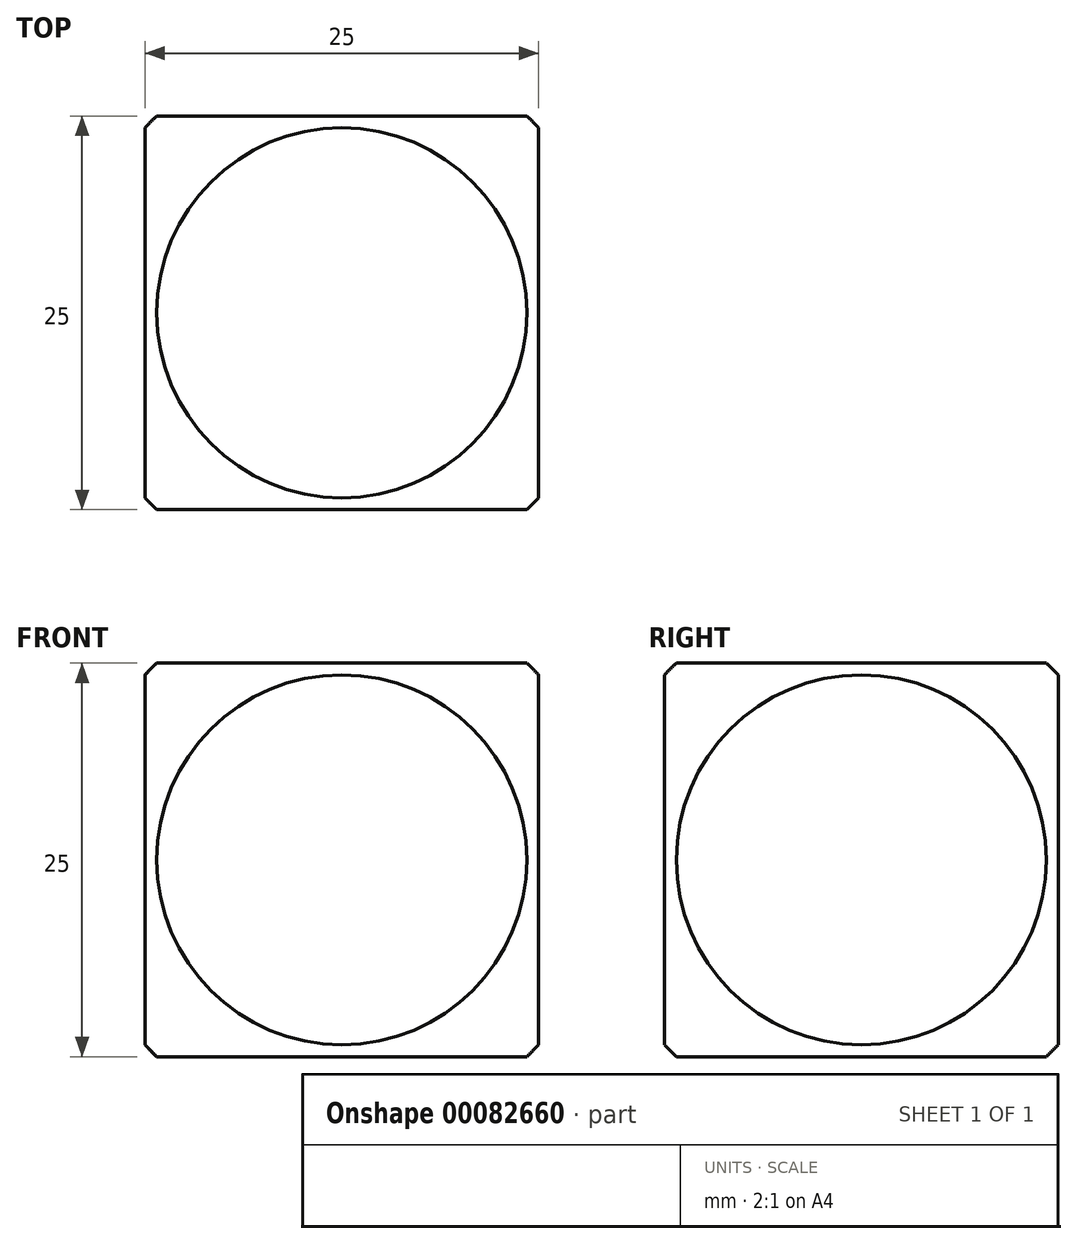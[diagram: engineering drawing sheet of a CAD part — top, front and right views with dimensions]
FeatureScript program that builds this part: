
annotation { "Feature Type Name" : "Feature", "Feature Type Description" : "" }
export const myFeature = defineFeature(function(context is Context, id is Id, definition is map)
    precondition{}
    {
        {
            var Q0;
            Q0=qCreatedBy(makeId("Front.planeOp"),FACE);
            var sketch = newSketch(context, id + "F0", { "sketchPlane" : qUnion([Q0])});
            skLineSegment(sketch, "E0.bottom", {"start": v(12.5, 12.5) * mm, "end": v(-12.5, 12.5) * mm});
            skLineSegment(sketch, "E0.top", {"start": v(12.5, -12.5) * mm, "end": v(-12.5, -12.5) * mm});
            skLineSegment(sketch, "E0.left", {"start": v(12.5, 12.5) * mm, "end": v(12.5, -12.5) * mm});
            skLineSegment(sketch, "E0.right", {"start": v(-12.5, 12.5) * mm, "end": v(-12.5, -12.5) * mm});
            skPoint(sketch, "E0.middle", {"position": v(0, 0) * mm});
            skSolve(sketch);
        }
        {
            var Q0;
            Q0 = qSketchRegion(id + "F0", true);
            extrude(context, id + "F1", {"entities" : qUnion([Q0]), "endBound" : BoundingType.SYMMETRIC, "depth" : 25 * mm});
        }
        {
            var Q0;
            Q0=qCreatedBy(makeId("Front.planeOp"),FACE);
            var sketch = newSketch(context, id + "F2", { "sketchPlane" : qUnion([Q0])});
            skLineSegment(sketch, "E1", {"start": v(0, 17.16) * mm, "end": v(0, -17.16) * mm});
            skArc(sketch, "E2", {"start": v(0, 17.16) * mm, "mid": v(-17.16, 0) * mm, "end": v(0, -17.16) * mm});
            skLineSegment(sketch, "E3", {"start": v(-12.5, 11.75) * mm, "end": v(-12.5, -11.75) * mm, "construction": true});
            skCircle(sketch, "E4", {"center": v(0, 0) * mm, "radius": 11.75 * mm, "construction": true});
            skLineSegment(sketch, "E5", {"start": v(-12.5, 11.75) * mm, "end": v(0, 11.75) * mm, "construction": true});
            skSolve(sketch);
        }
        {
            var Q0;
            Q0=makeQuery(id+"F2.imprint","IMPRINT",FACE,{"disambiguationData":[TD([[makeQuery(id+"F2.imprint","IMPRINT",EDGE,{"derivedFrom":sQuery(id+"F2.wireOp",EDGE,"E1")}),-1.0]])]});
            var Q1;
            Q1=sQuery(id+"F2.wireOp",EDGE,"E1");
            revolve(context, id + "F3", {"operationType" : NewBodyOperationType.INTERSECT, "entities" : qUnion([Q0]), "axis" : qUnion([Q1]), "revolveType" : RevolveType.FULL});
        }
    });
